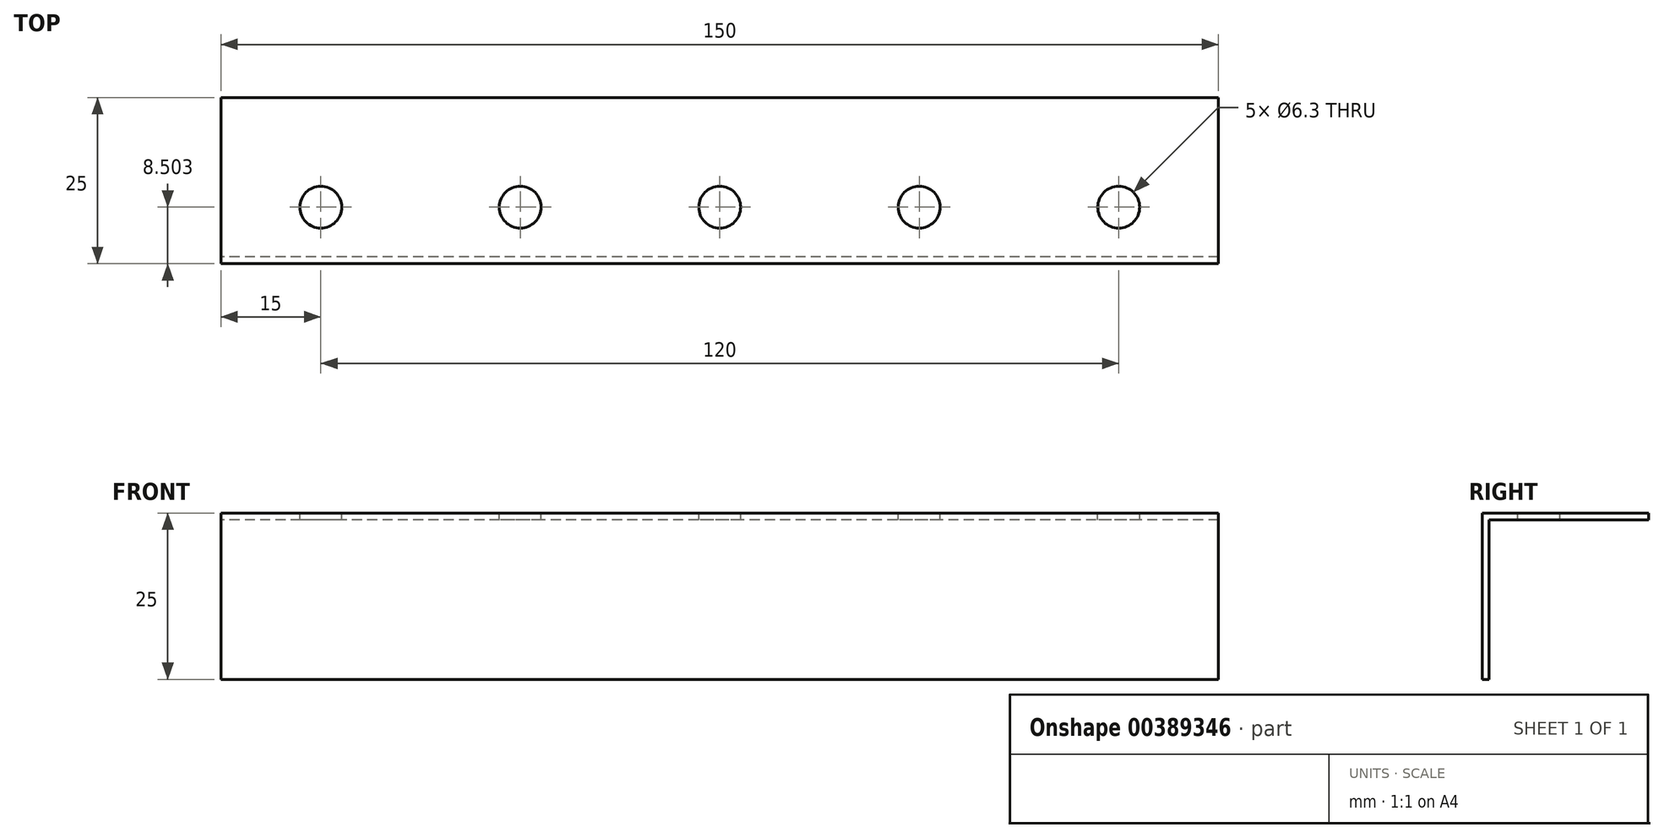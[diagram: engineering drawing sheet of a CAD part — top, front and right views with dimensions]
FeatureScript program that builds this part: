
annotation { "Feature Type Name" : "Feature", "Feature Type Description" : "" }
export const myFeature = defineFeature(function(context is Context, id is Id, definition is map)
    precondition{}
    {
        {
            var Q0;
            Q0=qCreatedBy(makeId("Right.planeOp"),FACE);
            var sketch = newSketch(context, id + "F0", { "sketchPlane" : qUnion([Q0])});
            skLineSegment(sketch, "E0.bottom", {"start": v(-5.47, -1.65) * mm, "end": v(-4.47, -1.65) * mm});
            skLineSegment(sketch, "E0.top", {"start": v(-5.47, 23.35) * mm, "end": v(-4.47, 23.35) * mm});
            skLineSegment(sketch, "E0.left", {"start": v(-5.47, -1.65) * mm, "end": v(-5.47, 23.35) * mm});
            skLineSegment(sketch, "E0.right", {"start": v(-4.47, -1.65) * mm, "end": v(-4.47, 23.35) * mm});
            skLineSegment(sketch, "E1.bottom", {"start": v(-5.47, 23.35) * mm, "end": v(19.53, 23.35) * mm});
            skLineSegment(sketch, "E1.top", {"start": v(-5.47, 22.35) * mm, "end": v(19.53, 22.35) * mm});
            skLineSegment(sketch, "E1.left", {"start": v(-5.47, 23.35) * mm, "end": v(-5.47, 22.35) * mm});
            skLineSegment(sketch, "E1.right", {"start": v(19.53, 23.35) * mm, "end": v(19.53, 22.35) * mm});
            skSolve(sketch);
        }
        {
            var Q0;
            Q0 = qSketchRegion(id + "F0", true);
            extrude(context, id + "F1", {"entities" : qUnion([Q0]), "depth" : 150 * mm, "offsetDistance" : 25 * mm});
        }
        {
            var Q0;
            Q0=makeQuery(id+"F1.opExtrude","SWEPT_FACE",FACE,{"disambiguationData":[OSD([sQuery(id+"F0.wireOp",EDGE,"E1.bottom")])]});
            var sketch = newSketch(context, id + "F2", { "sketchPlane" : qUnion([Q0])});
            skCircle(sketch, "E2", {"center": v(15, 3.03) * mm, "radius": 3.15 * mm});
            skCircle(sketch, "E3", {"center": v(45, 3.03) * mm, "radius": 3.15 * mm});
            skCircle(sketch, "E4", {"center": v(75, 3.03) * mm, "radius": 3.15 * mm});
            skCircle(sketch, "E5", {"center": v(105, 3.03) * mm, "radius": 3.15 * mm});
            skCircle(sketch, "E6", {"center": v(135, 3.03) * mm, "radius": 3.15 * mm});
            skSolve(sketch);
        }
        {
            var Q0;
            Q0 = qSketchRegion(id + "F2", true);
            extrude(context, id + "F3", {"entities" : qUnion([Q0]), "operationType" : NewBodyOperationType.REMOVE, "oppositeDirection" : true, "depth" : 1 * mm, "offsetDistance" : 25 * mm});
        }
    });
